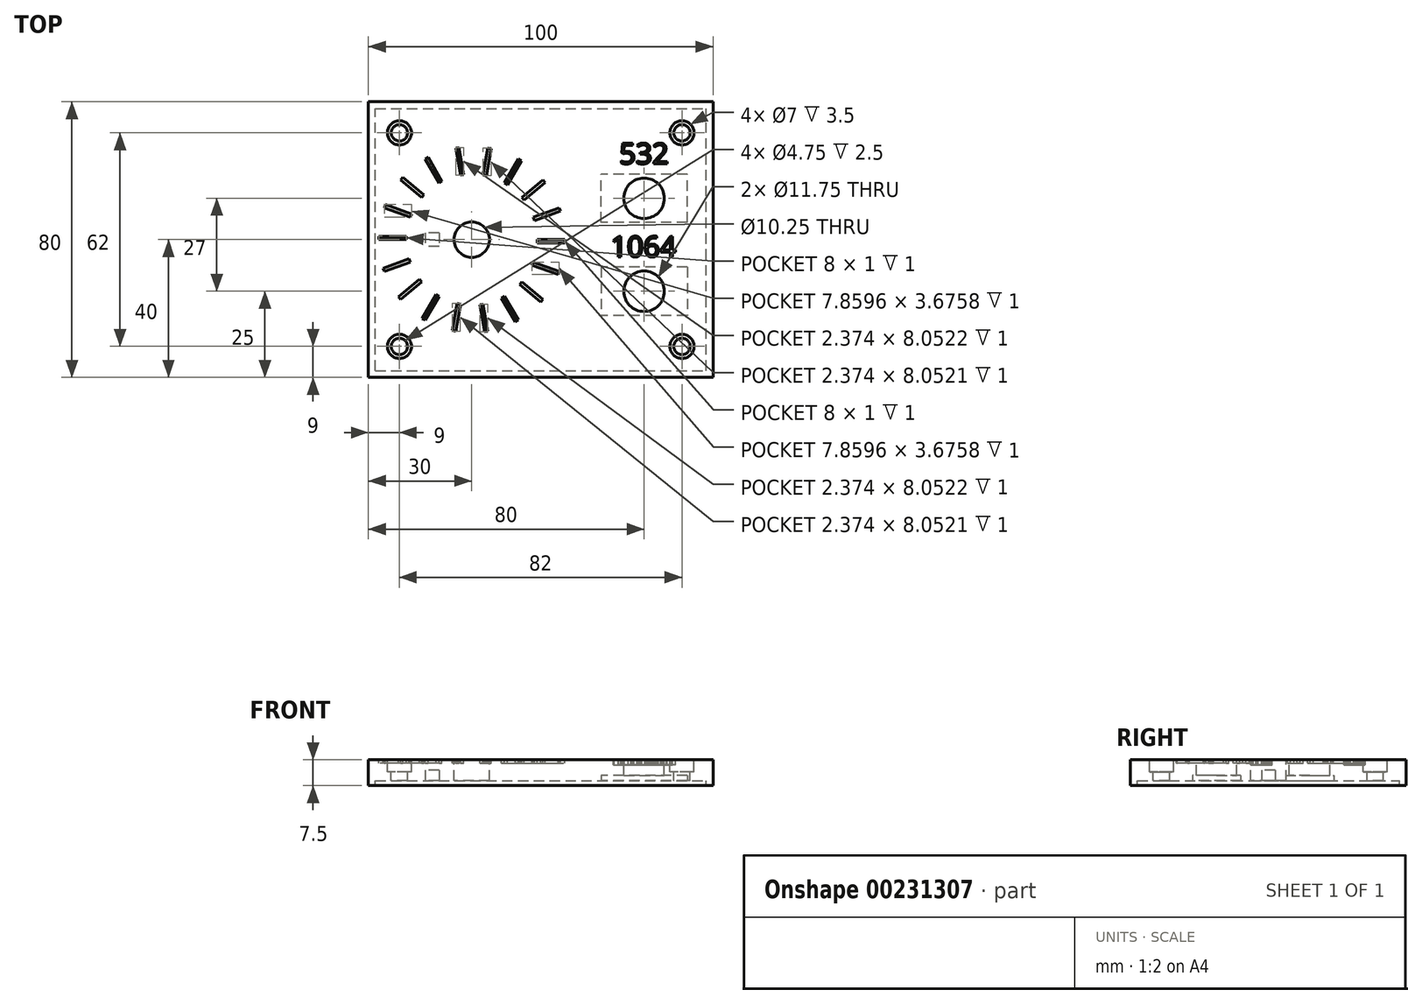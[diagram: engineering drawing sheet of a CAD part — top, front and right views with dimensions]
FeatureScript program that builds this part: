
annotation { "Feature Type Name" : "Feature", "Feature Type Description" : "" }
export const myFeature = defineFeature(function(context is Context, id is Id, definition is map)
    precondition{}
    {
        {
            var Q0;
            Q0=qCreatedBy(makeId("Top.planeOp"),FACE);
            var sketch = newSketch(context, id + "F0", { "sketchPlane" : qUnion([Q0])});
            skLineSegment(sketch, "E0.bottom", {"start": v(0, 0) * mm, "end": v(100, 0) * mm});
            skLineSegment(sketch, "E0.top", {"start": v(0, 80) * mm, "end": v(100, 80) * mm});
            skLineSegment(sketch, "E0.left", {"start": v(0, 0) * mm, "end": v(0, 80) * mm});
            skLineSegment(sketch, "E0.right", {"start": v(100, 0) * mm, "end": v(100, 80) * mm});
            skSolve(sketch);
        }
        {
            var Q0;
            Q0 = qSketchRegion(id + "F0", true);
            extrude(context, id + "F1", {"entities" : qUnion([Q0]), "depth" : 6 * mm});
        }
        {
            var Q0;
            Q0=makeQuery(id+"F1.opExtrude","CAP_FACE",FACE,{"disambiguationData":[OSD([sQuery(id+"F0.wireOp",EDGE,"E0.bottom"),sQuery(id+"F0.wireOp",EDGE,"E0.top"),sQuery(id+"F0.wireOp",EDGE,"E0.left"),sQuery(id+"F0.wireOp",EDGE,"E0.right")])],"isStart":false});
            var sketch = newSketch(context, id + "F2", { "sketchPlane" : qUnion([Q0])});
            skCircle(sketch, "E1", {"center": v(30, 40) * mm, "radius": 5.12 * mm});
            skPoint(sketch, "E1.centerSnap0", {"position": v(0, 40) * mm});
            skSolve(sketch);
        }
        {
            var Q0;
            Q0 = qSketchRegion(id + "F2", true);
            extrude(context, id + "F3", {"entities" : qUnion([Q0]), "operationType" : NewBodyOperationType.REMOVE, "oppositeDirection" : true, "depth" : 25 * mm});
        }
        {
            var Q0;
            Q0=makeQuery(id+"F1.opExtrude","CAP_FACE",FACE,{"disambiguationData":[OSD([sQuery(id+"F0.wireOp",EDGE,"E0.bottom"),sQuery(id+"F0.wireOp",EDGE,"E0.top"),sQuery(id+"F0.wireOp",EDGE,"E0.left"),sQuery(id+"F0.wireOp",EDGE,"E0.right")])],"isStart":false});
            var sketch = newSketch(context, id + "F4", { "sketchPlane" : qUnion([Q0])});
            skPoint(sketch, "E2.firstSnap0", {"position": v(0, 40) * mm});
            skLineSegment(sketch, "E2.bottom", {"start": v(11, 40) * mm, "end": v(3, 40) * mm});
            skLineSegment(sketch, "E2.top", {"start": v(11, 41) * mm, "end": v(3, 41) * mm});
            skLineSegment(sketch, "E2.left", {"start": v(11, 40) * mm, "end": v(11, 41) * mm});
            skLineSegment(sketch, "E2.right", {"start": v(3, 40) * mm, "end": v(3, 41) * mm});
            skPoint(sketch, "E3", {"position": v(30, 40) * mm});
            skLineSegment(sketch, "E4.1.0", {"start": v(12.15, 33.5) * mm, "end": v(4.63, 30.77) * mm});
            skLineSegment(sketch, "E4.1.1", {"start": v(12.15, 33.5) * mm, "end": v(11.8, 34.44) * mm});
            skLineSegment(sketch, "E4.1.2", {"start": v(11.8, 34.44) * mm, "end": v(4.29, 31.7) * mm});
            skLineSegment(sketch, "E4.1.3", {"start": v(4.63, 30.77) * mm, "end": v(4.29, 31.7) * mm});
            skLineSegment(sketch, "E4.2.0", {"start": v(15.45, 27.79) * mm, "end": v(9.32, 22.64) * mm});
            skLineSegment(sketch, "E4.2.1", {"start": v(15.45, 27.79) * mm, "end": v(14.8, 28.55) * mm});
            skLineSegment(sketch, "E4.2.2", {"start": v(14.8, 28.55) * mm, "end": v(8.67, 23.41) * mm});
            skLineSegment(sketch, "E4.2.3", {"start": v(9.32, 22.64) * mm, "end": v(8.67, 23.41) * mm});
            skLineSegment(sketch, "E4.3.0", {"start": v(20.5, 23.55) * mm, "end": v(16.5, 16.62) * mm});
            skLineSegment(sketch, "E4.3.1", {"start": v(20.5, 23.55) * mm, "end": v(19.63, 24.05) * mm});
            skLineSegment(sketch, "E4.3.2", {"start": v(19.63, 24.05) * mm, "end": v(15.63, 17.12) * mm});
            skLineSegment(sketch, "E4.3.3", {"start": v(16.5, 16.62) * mm, "end": v(15.63, 17.12) * mm});
            skLineSegment(sketch, "E4.4.0", {"start": v(26.7, 21.29) * mm, "end": v(25.31, 13.41) * mm});
            skLineSegment(sketch, "E4.4.1", {"start": v(26.7, 21.29) * mm, "end": v(25.72, 21.46) * mm});
            skLineSegment(sketch, "E4.4.2", {"start": v(25.72, 21.46) * mm, "end": v(24.33, 13.58) * mm});
            skLineSegment(sketch, "E4.4.3", {"start": v(25.31, 13.41) * mm, "end": v(24.33, 13.58) * mm});
            skLineSegment(sketch, "E4.5.0", {"start": v(33.3, 21.29) * mm, "end": v(34.69, 13.41) * mm});
            skLineSegment(sketch, "E4.5.1", {"start": v(33.3, 21.29) * mm, "end": v(32.31, 21.12) * mm});
            skLineSegment(sketch, "E4.5.2", {"start": v(32.31, 21.12) * mm, "end": v(33.7, 13.24) * mm});
            skLineSegment(sketch, "E4.5.3", {"start": v(34.69, 13.41) * mm, "end": v(33.7, 13.24) * mm});
            skLineSegment(sketch, "E4.6.0", {"start": v(39.5, 23.55) * mm, "end": v(43.5, 16.62) * mm});
            skLineSegment(sketch, "E4.6.1", {"start": v(39.5, 23.55) * mm, "end": v(38.63, 23.05) * mm});
            skLineSegment(sketch, "E4.6.2", {"start": v(38.63, 23.05) * mm, "end": v(42.63, 16.12) * mm});
            skLineSegment(sketch, "E4.6.3", {"start": v(43.5, 16.62) * mm, "end": v(42.63, 16.12) * mm});
            skLineSegment(sketch, "E4.7.0", {"start": v(44.55, 27.79) * mm, "end": v(50.68, 22.64) * mm});
            skLineSegment(sketch, "E4.7.1", {"start": v(44.55, 27.79) * mm, "end": v(43.91, 27.02) * mm});
            skLineSegment(sketch, "E4.7.2", {"start": v(43.91, 27.02) * mm, "end": v(50.04, 21.88) * mm});
            skLineSegment(sketch, "E4.7.3", {"start": v(50.68, 22.64) * mm, "end": v(50.04, 21.88) * mm});
            skLineSegment(sketch, "E4.8.0", {"start": v(47.85, 33.5) * mm, "end": v(55.37, 30.77) * mm});
            skLineSegment(sketch, "E4.8.1", {"start": v(47.85, 33.5) * mm, "end": v(47.51, 32.56) * mm});
            skLineSegment(sketch, "E4.8.2", {"start": v(47.51, 32.56) * mm, "end": v(55.03, 29.83) * mm});
            skLineSegment(sketch, "E4.8.3", {"start": v(55.37, 30.77) * mm, "end": v(55.03, 29.83) * mm});
            skLineSegment(sketch, "E4.9.0", {"start": v(49, 40) * mm, "end": v(57, 40) * mm});
            skLineSegment(sketch, "E4.9.1", {"start": v(49, 40) * mm, "end": v(49, 39) * mm});
            skLineSegment(sketch, "E4.9.2", {"start": v(49, 39) * mm, "end": v(57, 39) * mm});
            skLineSegment(sketch, "E4.9.3", {"start": v(57, 40) * mm, "end": v(57, 39) * mm});
            skLineSegment(sketch, "E4.10.0", {"start": v(47.85, 46.5) * mm, "end": v(55.37, 49.23) * mm});
            skLineSegment(sketch, "E4.10.1", {"start": v(47.85, 46.5) * mm, "end": v(48.2, 45.56) * mm});
            skLineSegment(sketch, "E4.10.2", {"start": v(48.2, 45.56) * mm, "end": v(55.71, 48.3) * mm});
            skLineSegment(sketch, "E4.10.3", {"start": v(55.37, 49.23) * mm, "end": v(55.71, 48.3) * mm});
            skLineSegment(sketch, "E4.11.0", {"start": v(44.55, 52.21) * mm, "end": v(50.68, 57.36) * mm});
            skLineSegment(sketch, "E4.11.1", {"start": v(44.55, 52.21) * mm, "end": v(45.2, 51.45) * mm});
            skLineSegment(sketch, "E4.11.2", {"start": v(45.2, 51.45) * mm, "end": v(51.33, 56.59) * mm});
            skLineSegment(sketch, "E4.11.3", {"start": v(50.68, 57.36) * mm, "end": v(51.33, 56.59) * mm});
            skLineSegment(sketch, "E4.12.0", {"start": v(39.5, 56.45) * mm, "end": v(43.5, 63.38) * mm});
            skLineSegment(sketch, "E4.12.1", {"start": v(39.5, 56.45) * mm, "end": v(40.37, 55.95) * mm});
            skLineSegment(sketch, "E4.12.2", {"start": v(40.37, 55.95) * mm, "end": v(44.37, 62.88) * mm});
            skLineSegment(sketch, "E4.12.3", {"start": v(43.5, 63.38) * mm, "end": v(44.37, 62.88) * mm});
            skLineSegment(sketch, "E4.13.0", {"start": v(33.3, 58.71) * mm, "end": v(34.69, 66.59) * mm});
            skLineSegment(sketch, "E4.13.1", {"start": v(33.3, 58.71) * mm, "end": v(34.28, 58.54) * mm});
            skLineSegment(sketch, "E4.13.2", {"start": v(34.28, 58.54) * mm, "end": v(35.67, 66.42) * mm});
            skLineSegment(sketch, "E4.13.3", {"start": v(34.69, 66.59) * mm, "end": v(35.67, 66.42) * mm});
            skLineSegment(sketch, "E4.14.0", {"start": v(26.7, 58.71) * mm, "end": v(25.31, 66.59) * mm});
            skLineSegment(sketch, "E4.14.1", {"start": v(26.7, 58.71) * mm, "end": v(27.69, 58.88) * mm});
            skLineSegment(sketch, "E4.14.2", {"start": v(27.69, 58.88) * mm, "end": v(26.3, 66.76) * mm});
            skLineSegment(sketch, "E4.14.3", {"start": v(25.31, 66.59) * mm, "end": v(26.3, 66.76) * mm});
            skLineSegment(sketch, "E4.15.0", {"start": v(20.5, 56.45) * mm, "end": v(16.5, 63.38) * mm});
            skLineSegment(sketch, "E4.15.1", {"start": v(20.5, 56.45) * mm, "end": v(21.37, 56.95) * mm});
            skLineSegment(sketch, "E4.15.2", {"start": v(21.37, 56.95) * mm, "end": v(17.37, 63.88) * mm});
            skLineSegment(sketch, "E4.15.3", {"start": v(16.5, 63.38) * mm, "end": v(17.37, 63.88) * mm});
            skLineSegment(sketch, "E4.16.0", {"start": v(15.45, 52.21) * mm, "end": v(9.32, 57.36) * mm});
            skLineSegment(sketch, "E4.16.1", {"start": v(15.45, 52.21) * mm, "end": v(16.09, 52.98) * mm});
            skLineSegment(sketch, "E4.16.2", {"start": v(16.09, 52.98) * mm, "end": v(9.96, 58.12) * mm});
            skLineSegment(sketch, "E4.16.3", {"start": v(9.32, 57.36) * mm, "end": v(9.96, 58.12) * mm});
            skLineSegment(sketch, "E4.17.0", {"start": v(12.15, 46.5) * mm, "end": v(4.63, 49.23) * mm});
            skLineSegment(sketch, "E4.17.1", {"start": v(12.15, 46.5) * mm, "end": v(12.49, 47.44) * mm});
            skLineSegment(sketch, "E4.17.2", {"start": v(12.49, 47.44) * mm, "end": v(4.97, 50.17) * mm});
            skLineSegment(sketch, "E4.17.3", {"start": v(4.63, 49.23) * mm, "end": v(4.97, 50.17) * mm});
            skSolve(sketch);
        }
        {
            var Q0;
            Q0 = qSketchRegion(id + "F4", true);
            extrude(context, id + "F5", {"entities" : qUnion([Q0]), "operationType" : NewBodyOperationType.REMOVE, "oppositeDirection" : true, "depth" : 1 * mm});
        }
        {
            var Q0;
            Q0=makeQuery(id+"F1.opExtrude","CAP_FACE",FACE,{"disambiguationData":[OSD([sQuery(id+"F0.wireOp",EDGE,"E0.bottom"),sQuery(id+"F0.wireOp",EDGE,"E0.top"),sQuery(id+"F0.wireOp",EDGE,"E0.left"),sQuery(id+"F0.wireOp",EDGE,"E0.right")])],"isStart":false});
            var sketch = newSketch(context, id + "F6", { "sketchPlane" : qUnion([Q0])});
            skPoint(sketch, "E5.centerSnap0", {"position": v(100, 40) * mm});
            skCircle(sketch, "E6", {"center": v(80, 25) * mm, "radius": 5.88 * mm});
            skCircle(sketch, "E7", {"center": v(80, 52) * mm, "radius": 5.88 * mm});
            skSolve(sketch);
        }
        {
            var Q0;
            Q0 = qSketchRegion(id + "F6", true);
            extrude(context, id + "F7", {"entities" : qUnion([Q0]), "operationType" : NewBodyOperationType.REMOVE, "endBound" : BoundingType.THROUGH_ALL, "oppositeDirection" : true, "depth" : 25 * mm});
        }
        {
            var Q0;
            Q0=makeQuery(id+"F1.opExtrude","CAP_FACE",FACE,{"disambiguationData":[OSD([sQuery(id+"F0.wireOp",EDGE,"E0.bottom"),sQuery(id+"F0.wireOp",EDGE,"E0.top"),sQuery(id+"F0.wireOp",EDGE,"E0.left"),sQuery(id+"F0.wireOp",EDGE,"E0.right")])],"isStart":true});
            var sketch = newSketch(context, id + "F8", { "sketchPlane" : qUnion([Q0])});
            skLineSegment(sketch, "E8.bottom", {"start": v(92.5, -45) * mm, "end": v(67.5, -45) * mm});
            skLineSegment(sketch, "E8.top", {"start": v(92.5, -59) * mm, "end": v(67.5, -59) * mm});
            skLineSegment(sketch, "E8.left", {"start": v(92.5, -45) * mm, "end": v(92.5, -59) * mm});
            skLineSegment(sketch, "E8.right", {"start": v(67.5, -45) * mm, "end": v(67.5, -59) * mm});
            skLineSegment(sketch, "E9.bottom", {"start": v(92.5, -32) * mm, "end": v(67.5, -32) * mm});
            skLineSegment(sketch, "E9.top", {"start": v(92.5, -18) * mm, "end": v(67.5, -18) * mm});
            skLineSegment(sketch, "E9.left", {"start": v(92.5, -32) * mm, "end": v(92.5, -18) * mm});
            skLineSegment(sketch, "E9.right", {"start": v(67.5, -32) * mm, "end": v(67.5, -18) * mm});
            skSolve(sketch);
        }
        {
            var Q0;
            Q0 = qSketchRegion(id + "F8", true);
            extrude(context, id + "F9", {"entities" : qUnion([Q0]), "operationType" : NewBodyOperationType.REMOVE, "oppositeDirection" : true, "depth" : 1.5 * mm});
        }
        {
            var Q0;
            Q0=makeQuery(id+"F1.opExtrude","CAP_FACE",FACE,{"disambiguationData":[OSD([sQuery(id+"F0.wireOp",EDGE,"E0.bottom"),sQuery(id+"F0.wireOp",EDGE,"E0.top"),sQuery(id+"F0.wireOp",EDGE,"E0.left"),sQuery(id+"F0.wireOp",EDGE,"E0.right")])],"isStart":false});
            var sketch = newSketch(context, id + "F10", { "sketchPlane" : qUnion([Q0])});
            skCircle(sketch, "E10", {"center": v(9, 9) * mm, "radius": 3.5 * mm});
            skCircle(sketch, "E11", {"center": v(91, 9) * mm, "radius": 3.5 * mm});
            skCircle(sketch, "E12", {"center": v(91, 71) * mm, "radius": 3.5 * mm});
            skCircle(sketch, "E13", {"center": v(9, 71) * mm, "radius": 3.5 * mm});
            skSolve(sketch);
        }
        {
            var Q0;
            Q0 = qSketchRegion(id + "F10", true);
            extrude(context, id + "F11", {"entities" : qUnion([Q0]), "operationType" : NewBodyOperationType.REMOVE, "oppositeDirection" : true, "depth" : 3.5 * mm});
        }
        {
            var Q0;
            Q0=makeQuery(id+"F1.opExtrude","CAP_FACE",FACE,{"disambiguationData":[OSD([sQuery(id+"F0.wireOp",EDGE,"E0.bottom"),sQuery(id+"F0.wireOp",EDGE,"E0.top"),sQuery(id+"F0.wireOp",EDGE,"E0.left"),sQuery(id+"F0.wireOp",EDGE,"E0.right")])],"isStart":false});
            var sketch = newSketch(context, id + "F12", { "sketchPlane" : qUnion([Q0])});
            skCircle(sketch, "E14", {"center": v(9, 71) * mm, "radius": 2.38 * mm});
            skCircle(sketch, "E15", {"center": v(9, 9) * mm, "radius": 2.38 * mm});
            skCircle(sketch, "E16", {"center": v(91, 9) * mm, "radius": 2.38 * mm});
            skCircle(sketch, "E17", {"center": v(91, 71) * mm, "radius": 2.38 * mm});
            skSolve(sketch);
        }
        {
            var Q0;
            Q0 = qSketchRegion(id + "F12", true);
            extrude(context, id + "F13", {"entities" : qUnion([Q0]), "operationType" : NewBodyOperationType.REMOVE, "endBound" : BoundingType.THROUGH_ALL, "oppositeDirection" : true, "depth" : 25 * mm});
        }
        {
            var Q0;
            Q0=makeQuery(id+"F1.opExtrude","CAP_FACE",FACE,{"disambiguationData":[OSD([sQuery(id+"F0.wireOp",EDGE,"E0.bottom"),sQuery(id+"F0.wireOp",EDGE,"E0.top"),sQuery(id+"F0.wireOp",EDGE,"E0.left"),sQuery(id+"F0.wireOp",EDGE,"E0.right")])],"isStart":false});
            var sketch = newSketch(context, id + "F14", { "sketchPlane" : qUnion([Q0])});
            skText(sketch, "E18", { "text": "532", "fontName": "OpenSans-Regular.ttf"});
            skText(sketch, "E19", { "text": "1064\n", "fontName": "OpenSans-Regular.ttf"});
            const initialGuessF14  = {"E18": [0.0728, 0.062, 1, 0, 0.006], "E19": [0.07028, 0.035, 1, 0, 0.006]};
            skSetInitialGuess(sketch, initialGuessF14);
            skSolve(sketch);
        }
        {
            var Q0;
            Q0 = qSketchRegion(id + "F14", true);
            extrude(context, id + "F15", {"entities" : qUnion([Q0]), "operationType" : NewBodyOperationType.REMOVE, "oppositeDirection" : true, "depth" : 1.5 * mm});
        }
        {
            var Q0;
            Q0=makeQuery(id+"F1.opExtrude","CAP_FACE",FACE,{"disambiguationData":[OSD([sQuery(id+"F0.wireOp",EDGE,"E0.bottom"),sQuery(id+"F0.wireOp",EDGE,"E0.top"),sQuery(id+"F0.wireOp",EDGE,"E0.left"),sQuery(id+"F0.wireOp",EDGE,"E0.right")])],"isStart":true});
            var sketch = newSketch(context, id + "F16", { "sketchPlane" : qUnion([Q0])});
            skLineSegment(sketch, "E20.bottom", {"start": v(2, -2) * mm, "end": v(98, -2) * mm});
            skLineSegment(sketch, "E20.top", {"start": v(2, -78) * mm, "end": v(98, -78) * mm});
            skLineSegment(sketch, "E20.left", {"start": v(2, -2) * mm, "end": v(2, -78) * mm});
            skLineSegment(sketch, "E20.right", {"start": v(98, -2) * mm, "end": v(98, -78) * mm});
            skLineSegment(sketch, "E21.bottom", {"start": v(0, -80) * mm, "end": v(100, -80) * mm});
            skLineSegment(sketch, "E21.top", {"start": v(0, 0) * mm, "end": v(100, 0) * mm});
            skLineSegment(sketch, "E21.left", {"start": v(0, -80) * mm, "end": v(0, 0) * mm});
            skLineSegment(sketch, "E21.right", {"start": v(100, -80) * mm, "end": v(100, 0) * mm});
            skSolve(sketch);
        }
        {
            var Q0;
            Q0 = qSketchRegion(id + "F16", true);
            extrude(context, id + "F17", {"entities" : qUnion([Q0]), "operationType" : NewBodyOperationType.ADD, "depth" : 1.5 * mm});
        }
        {
            var Q0;
            Q0=makeQuery(id+"F1.opExtrude","CAP_FACE",FACE,{"disambiguationData":[OSD([sQuery(id+"F0.wireOp",EDGE,"E0.bottom"),sQuery(id+"F0.wireOp",EDGE,"E0.top"),sQuery(id+"F0.wireOp",EDGE,"E0.left"),sQuery(id+"F0.wireOp",EDGE,"E0.right")])],"isStart":true});
            var sketch = newSketch(context, id + "F18", { "sketchPlane" : qUnion([Q0])});
            skLineSegment(sketch, "E22.bottom", {"start": v(20.5, -42) * mm, "end": v(16.5, -42) * mm});
            skLineSegment(sketch, "E22.top", {"start": v(20.5, -38) * mm, "end": v(16.5, -38) * mm});
            skLineSegment(sketch, "E22.left", {"start": v(20.5, -42) * mm, "end": v(20.5, -38) * mm});
            skLineSegment(sketch, "E22.right", {"start": v(16.5, -42) * mm, "end": v(16.5, -38) * mm});
            skLineSegment(sketch, "E23", {"start": v(2, -40) * mm, "end": v(30, -40) * mm, "construction": true});
            skSolve(sketch);
        }
        {
            var Q0;
            Q0 = qSketchRegion(id + "F18", true);
            extrude(context, id + "F19", {"entities" : qUnion([Q0]), "operationType" : NewBodyOperationType.REMOVE, "oppositeDirection" : true, "depth" : 3 * mm});
        }
    });
